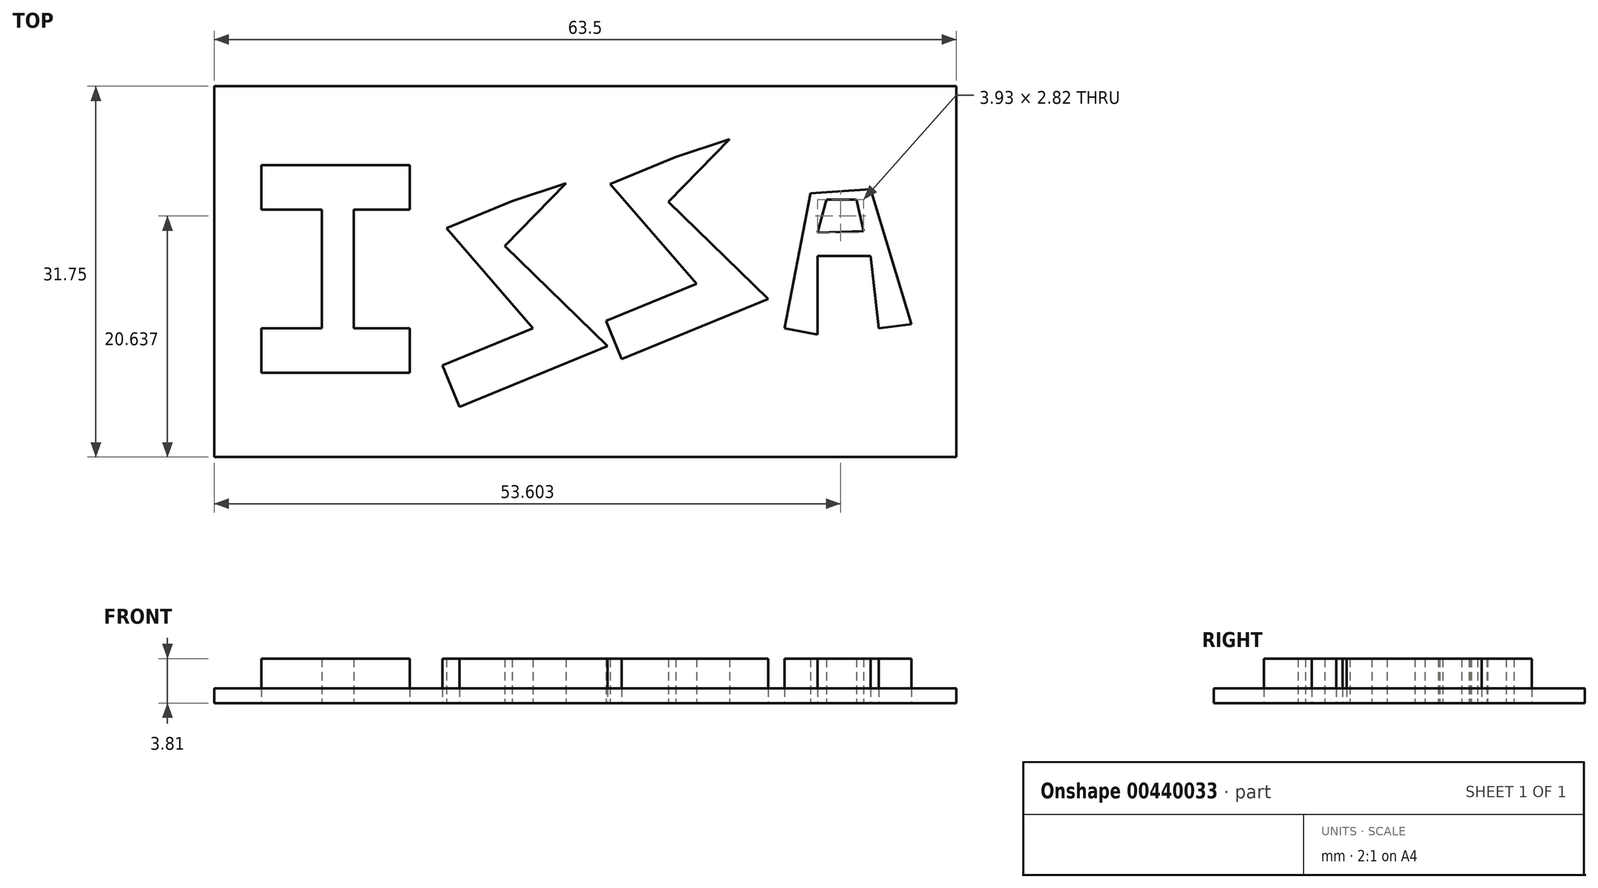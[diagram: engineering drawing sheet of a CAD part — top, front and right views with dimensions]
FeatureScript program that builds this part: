
annotation { "Feature Type Name" : "Feature", "Feature Type Description" : "" }
export const myFeature = defineFeature(function(context is Context, id is Id, definition is map)
    precondition{}
    {
        {
            var Q0;
            Q0=qCreatedBy(makeId("Top.planeOp"),FACE);
            var sketch = newSketch(context, id + "F0", { "sketchPlane" : qUnion([Q0])});
            skLineSegment(sketch, "E0.bottom", {"start": v(-15.65, 10.16) * mm, "end": v(-12.94, 10.16) * mm});
            skLineSegment(sketch, "E0.top", {"start": v(-15.65, 0) * mm, "end": v(-12.94, 0) * mm});
            skLineSegment(sketch, "E0.left", {"start": v(-15.65, 10.16) * mm, "end": v(-15.65, 0) * mm});
            skLineSegment(sketch, "E0.right", {"start": v(-12.94, 10.16) * mm, "end": v(-12.94, 0) * mm});
            skLineSegment(sketch, "E1.bottom", {"start": v(-20.84, 10.16) * mm, "end": v(-8.14, 10.16) * mm});
            skLineSegment(sketch, "E1.top", {"start": v(-20.84, 13.97) * mm, "end": v(-8.14, 13.97) * mm});
            skLineSegment(sketch, "E1.left", {"start": v(-20.84, 10.16) * mm, "end": v(-20.84, 13.97) * mm});
            skLineSegment(sketch, "E1.right", {"start": v(-8.14, 10.16) * mm, "end": v(-8.14, 13.97) * mm});
            skLineSegment(sketch, "E2.bottom", {"start": v(-20.84, 0) * mm, "end": v(-8.14, 0) * mm});
            skLineSegment(sketch, "E2.top", {"start": v(-20.84, -3.8) * mm, "end": v(-8.14, -3.8) * mm});
            skLineSegment(sketch, "E2.left", {"start": v(-20.84, 0) * mm, "end": v(-20.84, -3.8) * mm});
            skLineSegment(sketch, "E2.right", {"start": v(-8.14, 0) * mm, "end": v(-8.14, -3.8) * mm});
            skLineSegment(sketch, "E3", {"start": v(0.63, 10.86) * mm, "end": v(-4.99, 8.56) * mm});
            skLineSegment(sketch, "E4", {"start": v(-4.99, 8.56) * mm, "end": v(2.4, 0) * mm});
            skLineSegment(sketch, "E5", {"start": v(2.4, 0) * mm, "end": v(-5.36, -3.18) * mm});
            skLineSegment(sketch, "E6", {"start": v(-5.36, -3.18) * mm, "end": v(-3.9, -6.75) * mm});
            skLineSegment(sketch, "E7", {"start": v(-3.9, -6.75) * mm, "end": v(8.8, -1.54) * mm});
            skLineSegment(sketch, "E8", {"start": v(8.8, -1.54) * mm, "end": v(0, 7.03) * mm});
            skLineSegment(sketch, "E9", {"start": v(0, 7.03) * mm, "end": v(5.22, 12.39) * mm});
            skLineSegment(sketch, "E10", {"start": v(5.22, 12.39) * mm, "end": v(0.63, 10.86) * mm});
            skLineSegment(sketch, "E11", {"start": v(14.63, 14.65) * mm, "end": v(9.01, 12.35) * mm});
            skLineSegment(sketch, "E12", {"start": v(9.01, 12.35) * mm, "end": v(16.4, 3.79) * mm});
            skLineSegment(sketch, "E13", {"start": v(16.4, 3.79) * mm, "end": v(8.65, 0.6) * mm});
            skLineSegment(sketch, "E14", {"start": v(8.65, 0.6) * mm, "end": v(9.98, -2.65) * mm});
            skLineSegment(sketch, "E15", {"start": v(9.98, -2.65) * mm, "end": v(22.53, 2.5) * mm});
            skLineSegment(sketch, "E16", {"start": v(22.53, 2.5) * mm, "end": v(14, 10.82) * mm});
            skLineSegment(sketch, "E17", {"start": v(14, 10.82) * mm, "end": v(19.23, 16.18) * mm});
            skLineSegment(sketch, "E18", {"start": v(19.23, 16.18) * mm, "end": v(14.63, 14.65) * mm});
            skLineSegment(sketch, "E19", {"start": v(26.77, 8.19) * mm, "end": v(27.52, 11) * mm});
            skLineSegment(sketch, "E20", {"start": v(27.52, 11) * mm, "end": v(30.1, 11) * mm});
            skLineSegment(sketch, "E21", {"start": v(30.1, 11) * mm, "end": v(30.7, 8.3) * mm});
            skLineSegment(sketch, "E22", {"start": v(30.7, 8.3) * mm, "end": v(26.77, 8.19) * mm});
            skLineSegment(sketch, "E23", {"start": v(26.15, 11.53) * mm, "end": v(23.94, 0) * mm});
            skLineSegment(sketch, "E24", {"start": v(23.94, 0) * mm, "end": v(26.77, -0.54) * mm});
            skLineSegment(sketch, "E25", {"start": v(26.77, -0.54) * mm, "end": v(26.77, 6.18) * mm});
            skLineSegment(sketch, "E26", {"start": v(26.77, 6.18) * mm, "end": v(31.28, 6.18) * mm});
            skLineSegment(sketch, "E27", {"start": v(31.28, 6.18) * mm, "end": v(32, 0) * mm});
            skLineSegment(sketch, "E28", {"start": v(32, 0) * mm, "end": v(34.78, 0.32) * mm});
            skLineSegment(sketch, "E29", {"start": v(34.78, 0.32) * mm, "end": v(31.3, 11.88) * mm});
            skLineSegment(sketch, "E30", {"start": v(31.3, 11.88) * mm, "end": v(26.15, 11.53) * mm});
            skSolve(sketch);
        }
        {
            var Q0;
            Q0 = qSketchRegion(id + "F0", true);
            extrude(context, id + "F1", {"entities" : qUnion([Q0]), "depth" : 3.8 * mm});
        }
        {
            var Q0;
            Q0=qCreatedBy(makeId("Top.planeOp"),FACE);
            var sketch = newSketch(context, id + "F2", { "sketchPlane" : qUnion([Q0])});
            skLineSegment(sketch, "E31.bottom", {"start": v(-24.87, 20.71) * mm, "end": v(38.63, 20.71) * mm});
            skLineSegment(sketch, "E31.top", {"start": v(-24.87, -11.04) * mm, "end": v(38.63, -11.04) * mm});
            skLineSegment(sketch, "E31.left", {"start": v(-24.87, 20.71) * mm, "end": v(-24.87, -11.04) * mm});
            skLineSegment(sketch, "E31.right", {"start": v(38.63, 20.71) * mm, "end": v(38.63, -11.04) * mm});
            skSolve(sketch);
        }
        {
            var Q0;
            Q0 = qSketchRegion(id + "F2", true);
            extrude(context, id + "F3", {"entities" : qUnion([Q0]), "depth" : 1.27 * mm});
        }
    });
